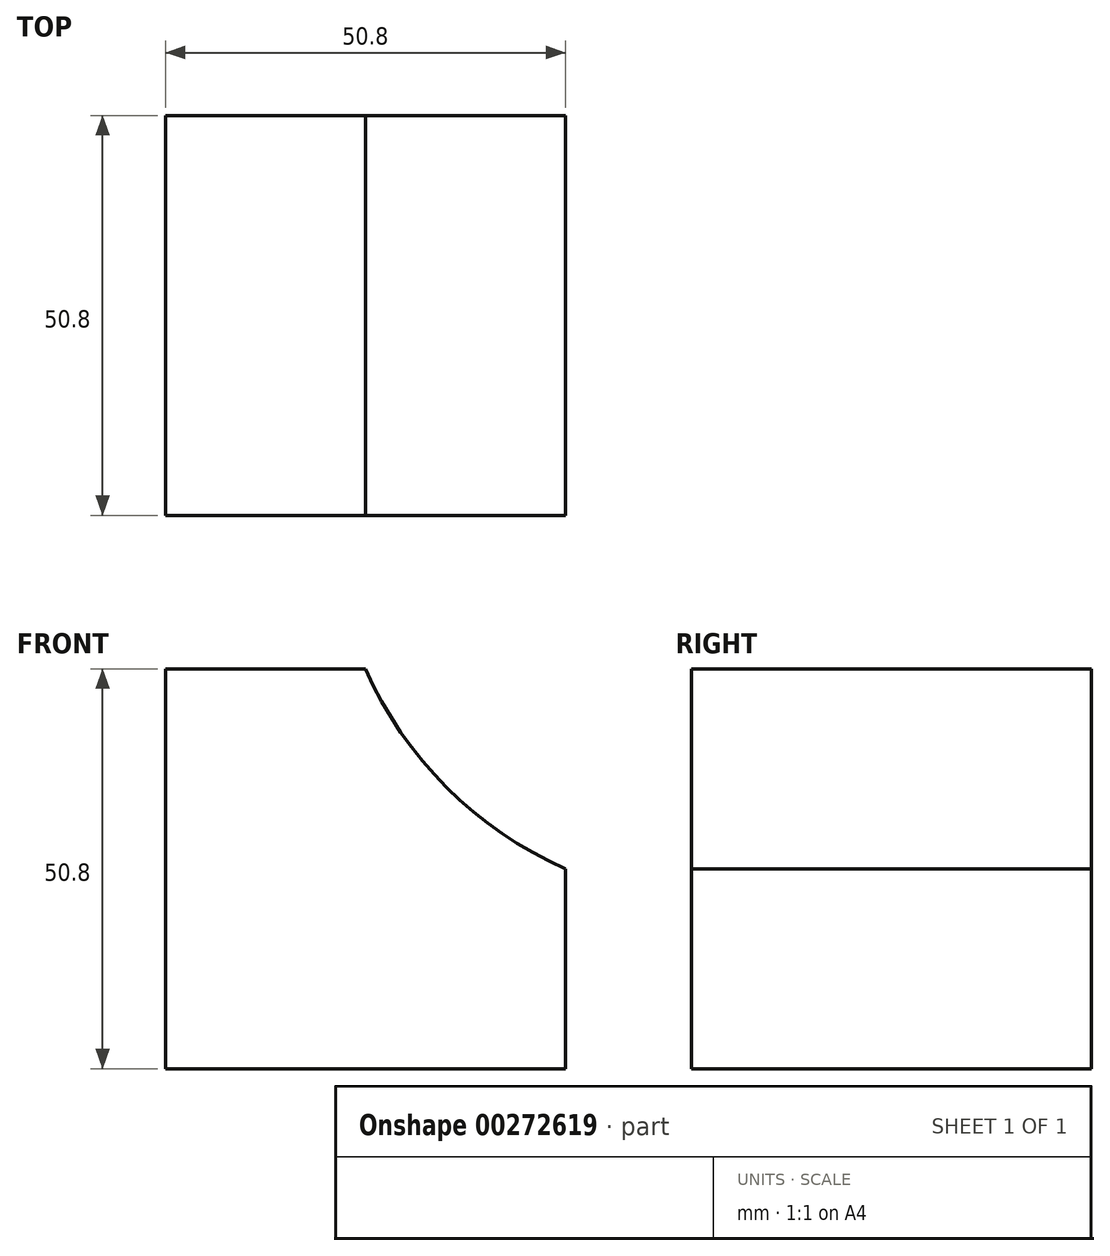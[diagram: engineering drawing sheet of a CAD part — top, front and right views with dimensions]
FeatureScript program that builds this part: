
annotation { "Feature Type Name" : "Feature", "Feature Type Description" : "" }
export const myFeature = defineFeature(function(context is Context, id is Id, definition is map)
    precondition{}
    {
        {
            var Q0;
            Q0=qCreatedBy(makeId("Front.planeOp"),FACE);
            var sketch = newSketch(context, id + "F0", { "sketchPlane" : qUnion([Q0])});
            skLineSegment(sketch, "E0", {"start": v(0, 0) * mm, "end": v(-50.8, 0) * mm});
            skLineSegment(sketch, "E1", {"start": v(-50.8, 0) * mm, "end": v(-50.8, 50.8) * mm});
            skLineSegment(sketch, "E2", {"start": v(-50.8, 50.8) * mm, "end": v(-25.4, 50.8) * mm});
            skLineSegment(sketch, "E3", {"start": v(0, 0) * mm, "end": v(0, 25.4) * mm});
            skArc(sketch, "E4", {"start": v(-25.4, 50.8) * mm, "mid": v(-15.1, 35.7) * mm, "end": v(0, 25.4) * mm});
            skSolve(sketch);
        }
        {
            var Q0;
            Q0 = qSketchRegion(id + "F0", true);
            extrude(context, id + "F1", {"entities" : qUnion([Q0]), "depth" : 50.8 * mm});
        }
    });
